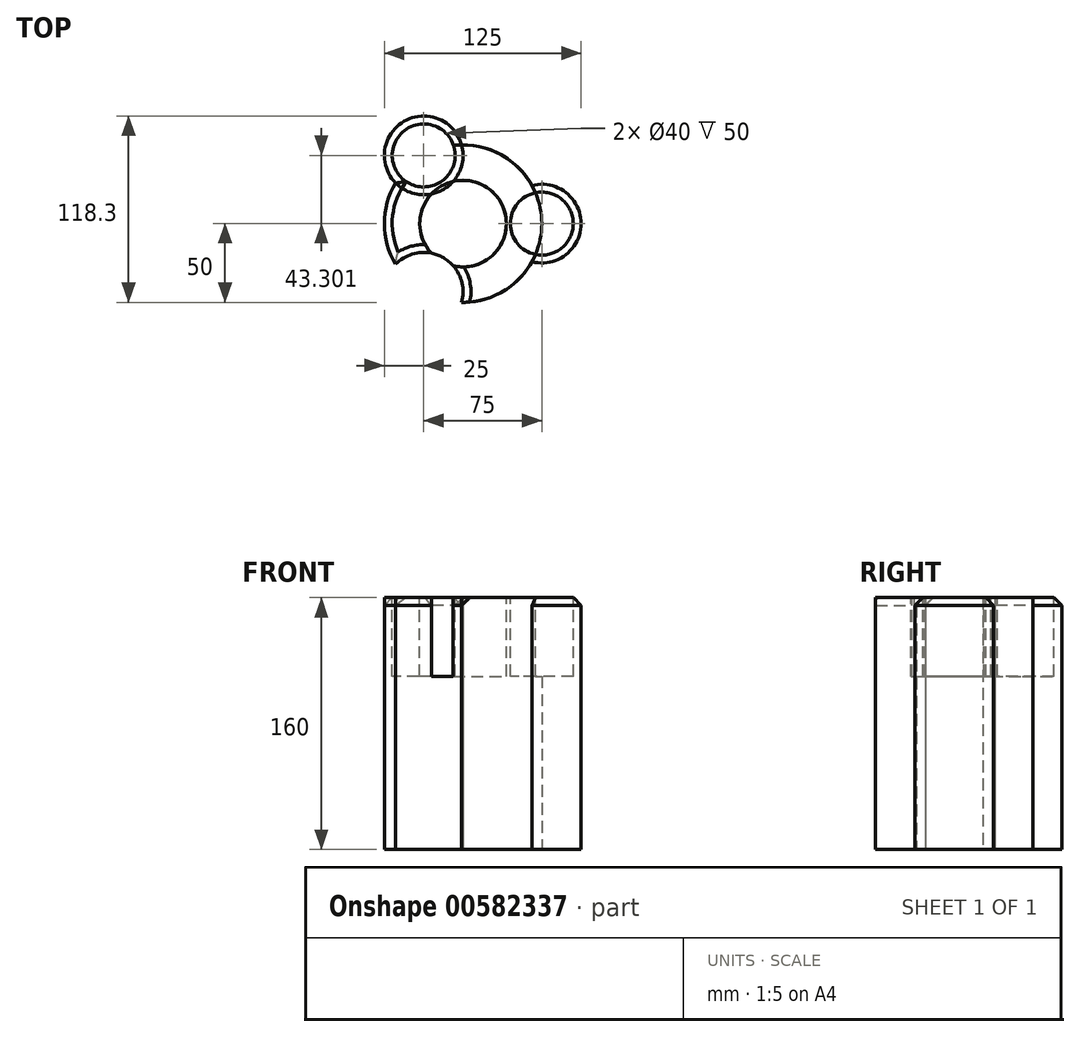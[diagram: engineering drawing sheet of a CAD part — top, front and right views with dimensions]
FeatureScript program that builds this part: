
annotation { "Feature Type Name" : "Feature", "Feature Type Description" : "" }
export const myFeature = defineFeature(function(context is Context, id is Id, definition is map)
    precondition{}
    {
        {
            var Q0;
            Q0=qCreatedBy(makeId("Top.planeOp"),FACE);
            var sketch = newSketch(context, id + "F0", { "sketchPlane" : qUnion([Q0])});
            skCircle(sketch, "E0", {"center": v(0, 0) * mm, "radius": 50 * mm});
            skPoint(sketch, "E1", {"position": v(50, 0) * mm});
            skCircle(sketch, "E2", {"center": v(50, 0) * mm, "radius": 25 * mm});
            skCircle(sketch, "E3.1.1", {"center": v(-25, 43.3) * mm, "radius": 25 * mm});
            skCircle(sketch, "E3.2.1", {"center": v(-25, -43.3) * mm, "radius": 25 * mm});
            skSolve(sketch);
        }
        {
            var Q0;
            {var subQ0=sQuery(id+"F0.wireOp",EDGE,"E2");var subQ1=sQuery(id+"F0.wireOp",EDGE,"E0");var subQ2=makeQuery(id+"F0.imprint","INTERSECT",VERTEX,{"disambiguationData":[OD(0.0)],"derivedFrom":[subQ1,subQ0]});Q0=makeQuery(id+"F0.imprint","IMPRINT",FACE,{"disambiguationData":[TD([[makeQuery(id+"F0.imprint","IMPRINT",EDGE,{"disambiguationData":[TD([[subQ2,-1.0]])],"derivedFrom":subQ1}),-1.0]])]});}
            var Q1;
            {var subQ0=sQuery(id+"F0.wireOp",EDGE,"E2");var subQ1=sQuery(id+"F0.wireOp",EDGE,"E0");var subQ2=makeQuery(id+"F0.imprint","INTERSECT",VERTEX,{"disambiguationData":[OD(0.0)],"derivedFrom":[subQ1,subQ0]});Q1=makeQuery(id+"F0.imprint","IMPRINT",FACE,{"disambiguationData":[TD([[makeQuery(id+"F0.imprint","IMPRINT",EDGE,{"disambiguationData":[TD([[subQ2,-1.0]])],"derivedFrom":subQ1}),1.0]])]});}
            var Q2;
            {var subQ0=sQuery(id+"F0.wireOp",EDGE,"E2");var subQ1=sQuery(id+"F0.wireOp",EDGE,"E0");var subQ2=makeQuery(id+"F0.imprint","INTERSECT",VERTEX,{"disambiguationData":[OD(0.0)],"derivedFrom":[subQ1,subQ0]});Q2=makeQuery(id+"F0.imprint","IMPRINT",FACE,{"disambiguationData":[TD([[makeQuery(id+"F0.imprint","IMPRINT",EDGE,{"disambiguationData":[TD([[subQ2,1.0]])],"derivedFrom":subQ1}),1.0]])]});}
            extrude(context, id + "F1", {"entities" : qUnion([Q0, Q1, Q2]), "depth" : 160 * mm, "offsetDistance" : 25 * mm});
        }
        {
            var Q0;
            {var subQ0=sQuery(id+"F0.wireOp",EDGE,"E0");var subQ1=sQuery(id+"F0.wireOp",EDGE,"E3.1.1");var subQ2=makeQuery(id+"F0.imprint","INTERSECT",VERTEX,{"disambiguationData":[OD(0.0)],"derivedFrom":[subQ1,subQ0]});Q0=makeQuery(id+"F0.imprint","IMPRINT",FACE,{"disambiguationData":[TD([[makeQuery(id+"F0.imprint","IMPRINT",EDGE,{"disambiguationData":[TD([[subQ2,-1.0]])],"derivedFrom":subQ1}),1.0]])]});}
            var Q1;
            {var subQ0=sQuery(id+"F0.wireOp",EDGE,"E0");var subQ1=sQuery(id+"F0.wireOp",EDGE,"E3.1.1");var subQ2=makeQuery(id+"F0.imprint","INTERSECT",VERTEX,{"disambiguationData":[OD(0.0)],"derivedFrom":[subQ1,subQ0]});Q1=makeQuery(id+"F0.imprint","IMPRINT",FACE,{"disambiguationData":[TD([[makeQuery(id+"F0.imprint","IMPRINT",EDGE,{"disambiguationData":[TD([[subQ2,1.0]])],"derivedFrom":subQ1}),1.0]])]});}
            var Q2;
            {var subQ0=sQuery(id+"F0.wireOp",EDGE,"E0");var subQ1=sQuery(id+"F0.wireOp",EDGE,"E2");var subQ5=makeQuery(id+"F0.imprint","INTERSECT",VERTEX,{"disambiguationData":[OD(0.0)],"derivedFrom":[subQ1,subQ0]});Q2=makeQuery(id+"F0.imprint","IMPRINT",FACE,{"disambiguationData":[TD([[makeQuery(id+"F0.imprint","IMPRINT",EDGE,{"disambiguationData":[TD([[subQ5,1.0]])],"derivedFrom":subQ1}),-1.0]])]});}
            var Q3;
            {var subQ0=sQuery(id+"F0.wireOp",EDGE,"E0");var subQ1=sQuery(id+"F0.wireOp",EDGE,"E2");var subQ2=makeQuery(id+"F0.imprint","INTERSECT",VERTEX,{"disambiguationData":[OD(0.0)],"derivedFrom":[subQ1,subQ0]});Q3=makeQuery(id+"F0.imprint","IMPRINT",FACE,{"disambiguationData":[TD([[makeQuery(id+"F0.imprint","IMPRINT",EDGE,{"disambiguationData":[TD([[subQ2,1.0]])],"derivedFrom":subQ1}),1.0]])]});}
            var Q4;
            {var subQ0=sQuery(id+"F0.wireOp",EDGE,"E0");var subQ1=sQuery(id+"F0.wireOp",EDGE,"E2");var subQ2=makeQuery(id+"F0.imprint","INTERSECT",VERTEX,{"disambiguationData":[OD(0.0)],"derivedFrom":[subQ1,subQ0]});Q4=makeQuery(id+"F0.imprint","IMPRINT",FACE,{"disambiguationData":[TD([[makeQuery(id+"F0.imprint","IMPRINT",EDGE,{"disambiguationData":[TD([[subQ2,-1.0]])],"derivedFrom":subQ1}),1.0]])]});}
            var Q5;
            {var subQ0=sQuery(id+"F0.wireOp",EDGE,"E3.2.1");var subQ1=sQuery(id+"F0.wireOp",EDGE,"E0");var subQ2=makeQuery(id+"F0.imprint","INTERSECT",VERTEX,{"disambiguationData":[OD(0.0)],"derivedFrom":[subQ1,subQ0]});Q5=makeQuery(id+"F0.imprint","IMPRINT",FACE,{"disambiguationData":[TD([[makeQuery(id+"F0.imprint","IMPRINT",EDGE,{"disambiguationData":[TD([[subQ2,1.0]])],"derivedFrom":subQ1}),1.0]])]});}
            var Q6;
            {var subQ0=sQuery(id+"F0.wireOp",EDGE,"E3.2.1");var subQ1=sQuery(id+"F0.wireOp",EDGE,"E0");var subQ2=makeQuery(id+"F0.imprint","INTERSECT",VERTEX,{"disambiguationData":[OD(0.0)],"derivedFrom":[subQ1,subQ0]});Q6=makeQuery(id+"F0.imprint","IMPRINT",FACE,{"disambiguationData":[TD([[makeQuery(id+"F0.imprint","IMPRINT",EDGE,{"disambiguationData":[TD([[subQ2,1.0]])],"derivedFrom":subQ1}),-1.0]])]});}
            extrude(context, id + "F2", {"entities" : qUnion([Q0, Q1, Q2, Q3, Q4, Q5, Q6]), "depth" : 160 * mm, "offsetDistance" : 25 * mm});
        }
        {
            var Q0;
            Q0=makeQuery(id+"F2.opExtrude","CAP_FACE",FACE,{"disambiguationData":[OSD([sQuery(id+"F0.wireOp",EDGE,"E2"),sQuery(id+"F0.wireOp",EDGE,"E3.1.1"),sQuery(id+"F0.wireOp",EDGE,"E0"),sQuery(id+"F0.wireOp",EDGE,"E3.2.1")])],"isStart":false});
            var sketch = newSketch(context, id + "F3", { "sketchPlane" : qUnion([Q0])});
            skPoint(sketch, "E4", {"position": v(-25, -43.3) * mm});
            skPoint(sketch, "E5", {"position": v(-25, 43.3) * mm});
            skPoint(sketch, "E6", {"position": v(50, 0) * mm});
            skCircle(sketch, "E7", {"center": v(-25, 43.3) * mm, "radius": 20 * mm});
            skCircle(sketch, "E8", {"center": v(-25, -43.3) * mm, "radius": 20 * mm});
            skCircle(sketch, "E9", {"center": v(50, 0) * mm, "radius": 20 * mm});
            skCircle(sketch, "E10", {"center": v(0, 0) * mm, "radius": 27.5 * mm});
            skSolve(sketch);
        }
        {
            var Q0;
            Q0 = qSketchRegion(id + "F3", true);
            extrude(context, id + "F4", {"entities" : qUnion([Q0]), "operationType" : NewBodyOperationType.REMOVE, "oppositeDirection" : true, "depth" : 50 * mm, "offsetDistance" : 25 * mm});
        }
        {
            var Q0;
            {var subQ0=sQuery(id+"F0.wireOp",EDGE,"E0");Q0=makeQuery(id+"F2.opExtrude","CAP_EDGE",EDGE,{"disambiguationData":[OSD([subQ0]),TDD([makeQuery(id+"F0.imprint","IMPRINT",EDGE,{"disambiguationData":[TD([[makeQuery(id+"F0.imprint","INTERSECT",VERTEX,{"disambiguationData":[OD(0.0)],"derivedFrom":[sQuery(id+"F0.wireOp",EDGE,"E2"),subQ0]}),1.0]])],"derivedFrom":subQ0})])],"isStart":false});}
            var Q1;
            Q1=makeQuery(id+"F2.opExtrude","CAP_EDGE",EDGE,{"disambiguationData":[OSD([sQuery(id+"F0.wireOp",EDGE,"E3.2.1")])],"isStart":false});
            var Q2;
            {var subQ0=sQuery(id+"F0.wireOp",EDGE,"E0");Q2=makeQuery(id+"F2.opExtrude","CAP_EDGE",EDGE,{"disambiguationData":[OSD([subQ0]),TDD([makeQuery(id+"F0.imprint","IMPRINT",EDGE,{"disambiguationData":[TD([[makeQuery(id+"F0.imprint","INTERSECT",VERTEX,{"disambiguationData":[OD(1.0)],"derivedFrom":[sQuery(id+"F0.wireOp",EDGE,"E3.1.1"),subQ0]}),-1.0]])],"derivedFrom":subQ0})])],"isStart":false});}
            var Q3;
            Q3=makeQuery(id+"F2.opExtrude","CAP_EDGE",EDGE,{"disambiguationData":[OSD([sQuery(id+"F0.wireOp",EDGE,"E3.1.1")])],"isStart":false});
            var Q4;
            {var subQ0=sQuery(id+"F0.wireOp",EDGE,"E0");Q4=makeQuery(id+"F2.opExtrude","CAP_EDGE",EDGE,{"disambiguationData":[OSD([subQ0]),TDD([makeQuery(id+"F0.imprint","IMPRINT",EDGE,{"disambiguationData":[TD([[makeQuery(id+"F0.imprint","INTERSECT",VERTEX,{"disambiguationData":[OD(1.0)],"derivedFrom":[sQuery(id+"F0.wireOp",EDGE,"E2"),subQ0]}),-1.0]])],"derivedFrom":subQ0})])],"isStart":false});}
            var Q5;
            Q5=makeQuery(id+"F2.opExtrude","CAP_EDGE",EDGE,{"disambiguationData":[OSD([sQuery(id+"F0.wireOp",EDGE,"E2")])],"isStart":false});
            chamfer(context, id + "F5", {"entities" : qUnion([Q0, Q1, Q2, Q3, Q4, Q5]), "width" : 5 * mm, "tangentPropagation" : true});
        }
    });
